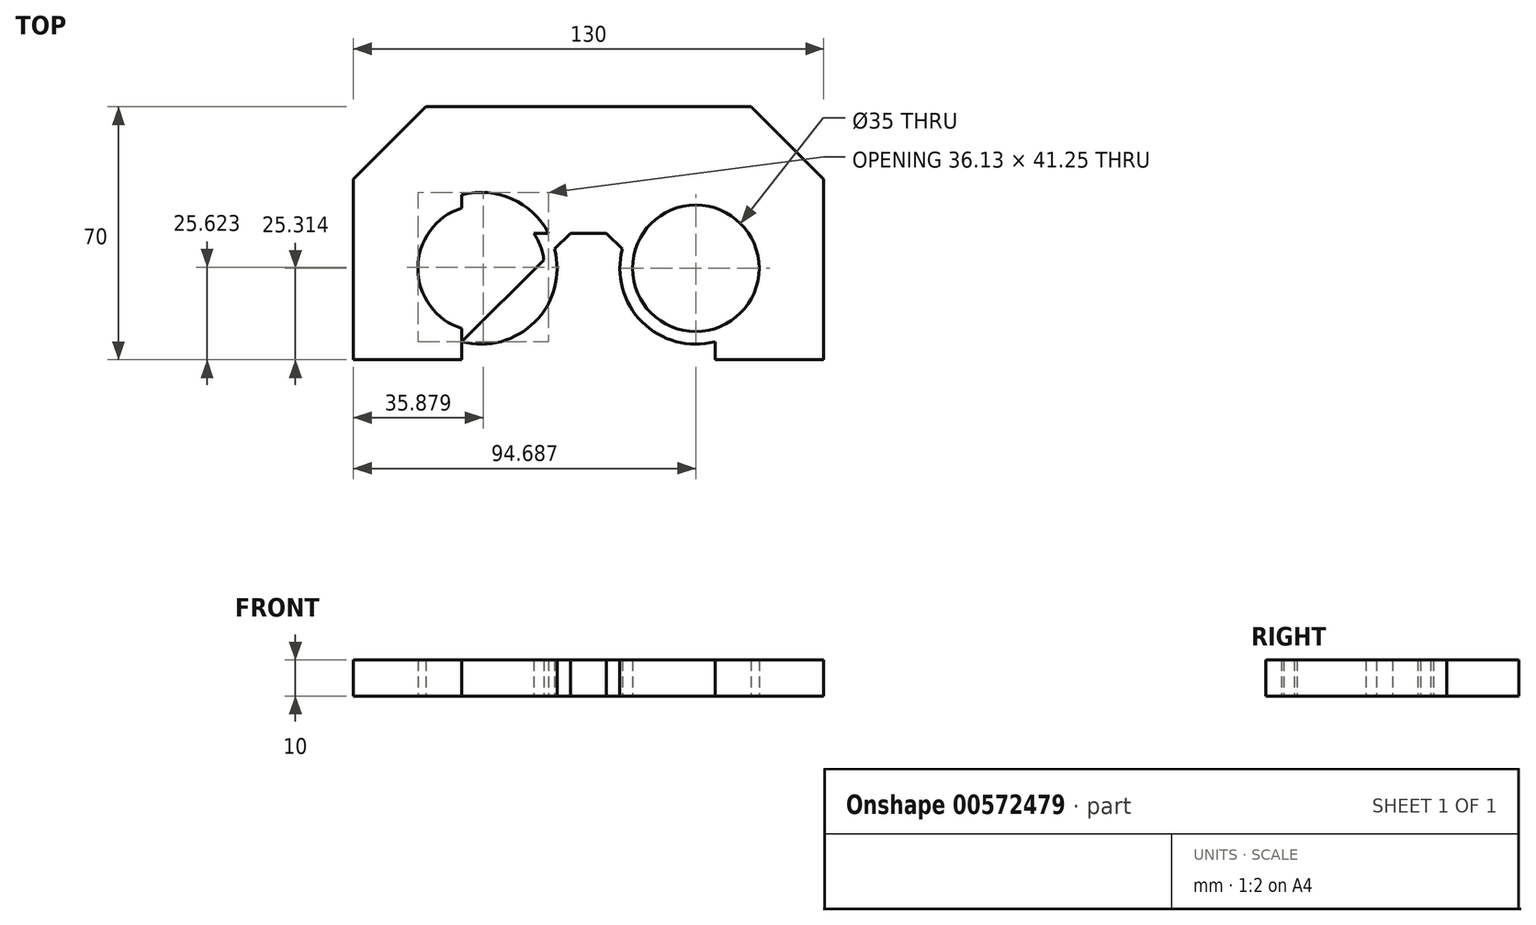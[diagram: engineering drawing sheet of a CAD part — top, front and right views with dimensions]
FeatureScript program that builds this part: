
annotation { "Feature Type Name" : "Feature", "Feature Type Description" : "" }
export const myFeature = defineFeature(function(context is Context, id is Id, definition is map)
    precondition{}
    {
        {
            var Q0;
            Q0=qCreatedBy(makeId("Top.planeOp"),FACE);
            var sketch = newSketch(context, id + "F0", { "sketchPlane" : qUnion([Q0])});
            skLineSegment(sketch, "E0.bottom", {"start": v(0, 0) * mm, "end": v(45, 0) * mm});
            skLineSegment(sketch, "E0.top", {"start": v(0, -35) * mm, "end": v(45, -35) * mm});
            skLineSegment(sketch, "E0.left", {"start": v(0, 0) * mm, "end": v(0, -35) * mm});
            skLineSegment(sketch, "E0.right", {"start": v(45, 0) * mm, "end": v(45, -35) * mm});
            skLineSegment(sketch, "E1.bottom", {"start": v(35, -20) * mm, "end": v(65, -20) * mm});
            skLineSegment(sketch, "E1.top", {"start": v(35, -70) * mm, "end": v(65, -70) * mm});
            skLineSegment(sketch, "E1.left", {"start": v(35, -20) * mm, "end": v(35, -70) * mm});
            skLineSegment(sketch, "E1.right", {"start": v(65, -20) * mm, "end": v(65, -70) * mm});
            skLineSegment(sketch, "E2", {"start": v(5, -35) * mm, "end": v(35, -65) * mm});
            skLineSegment(sketch, "E3", {"start": v(45, 0) * mm, "end": v(65, -20) * mm});
            skCircle(sketch, "E4", {"center": v(29.69, -44.69) * mm, "radius": 17.5 * mm});
            skCircle(sketch, "E5", {"center": v(29.69, -44.69) * mm, "radius": 21 * mm});
            skLineSegment(sketch, "E6.MirrorCS", {"start": v(-45, 0) * mm, "end": v(-45, -35) * mm});
            skCircle(sketch, "E7.MirrorC", {"center": v(-29.69, -44.69) * mm, "radius": 21 * mm});
            skCircle(sketch, "E8.MirrorC", {"center": v(-29.69, -44.69) * mm, "radius": 17.5 * mm});
            skLineSegment(sketch, "E9.MirrorCS", {"start": v(-45, 0) * mm, "end": v(-65, -20) * mm});
            skLineSegment(sketch, "E10.MirrorCS", {"start": v(-5, -35) * mm, "end": v(-35, -65) * mm});
            skLineSegment(sketch, "E11.MirrorCS", {"start": v(-65, -20) * mm, "end": v(-65, -70) * mm});
            skLineSegment(sketch, "E12.MirrorCS", {"start": v(-35, -20) * mm, "end": v(-35, -70) * mm});
            skLineSegment(sketch, "E13.MirrorCS", {"start": v(-35, -20) * mm, "end": v(-65, -20) * mm});
            skLineSegment(sketch, "E14.MirrorCS", {"start": v(0, 0) * mm, "end": v(-45, 0) * mm});
            skLineSegment(sketch, "E15.MirrorCS", {"start": v(0, -35) * mm, "end": v(-45, -35) * mm});
            skLineSegment(sketch, "E16.MirrorCS", {"start": v(-35, -70) * mm, "end": v(-65, -70) * mm});
            skSolve(sketch);
        }
        {
            var Q0;
            Q0 = qSketchRegion(id + "F0", true);
            var Q1;
            {var subQ0=sQuery(id+"F0.wireOp",EDGE,"E13.MirrorCS");var subQ1=sQuery(id+"F0.wireOp",EDGE,"E6.MirrorCS");var subQ2=makeQuery(id+"F0.imprint","INTERSECT",VERTEX,{"derivedFrom":[subQ1,subQ0]});Q1=makeQuery(id+"F0.imprint","IMPRINT",FACE,{"disambiguationData":[TD([[makeQuery(id+"F0.imprint","IMPRINT",EDGE,{"disambiguationData":[TD([[subQ2,-1.0]])],"derivedFrom":subQ1}),1.0]])]});}
            var Q2;
            {var subQ5=sQuery(id+"F0.wireOp",EDGE,"E15.MirrorCS");var subQ7=sQuery(id+"F0.wireOp",EDGE,"E6.MirrorCS");var subQ9=makeQuery(id+"F0.imprint","INTERSECT",VERTEX,{"derivedFrom":[subQ7,subQ5]});Q2=makeQuery(id+"F0.imprint","IMPRINT",FACE,{"disambiguationData":[TD([[makeQuery(id+"F0.imprint","IMPRINT",EDGE,{"disambiguationData":[TD([[subQ9,1.0]])],"derivedFrom":subQ7}),1.0]])]});}
            var Q3;
            {var subQ0=sQuery(id+"F0.wireOp",EDGE,"E12.MirrorCS");var subQ1=sQuery(id+"F0.wireOp",EDGE,"E7.MirrorC");var subQ2=makeQuery(id+"F0.imprint","INTERSECT",VERTEX,{"disambiguationData":[OD(1.0)],"derivedFrom":[subQ1,subQ0]});Q3=makeQuery(id+"F0.imprint","IMPRINT",FACE,{"disambiguationData":[TD([[makeQuery(id+"F0.imprint","IMPRINT",EDGE,{"disambiguationData":[TD([[subQ2,-1.0]])],"derivedFrom":subQ1}),-1.0]])]});}
            var Q4;
            {var subQ0=sQuery(id+"F0.wireOp",EDGE,"E10.MirrorCS");var subQ1=sQuery(id+"F0.wireOp",EDGE,"E8.MirrorC");var subQ2=makeQuery(id+"F0.imprint","INTERSECT",VERTEX,{"disambiguationData":[OD(1.0)],"derivedFrom":[subQ1,subQ0]});Q4=makeQuery(id+"F0.imprint","IMPRINT",FACE,{"disambiguationData":[TD([[makeQuery(id+"F0.imprint","IMPRINT",EDGE,{"disambiguationData":[TD([[subQ2,-1.0]])],"derivedFrom":subQ1}),1.0]])]});}
            var Q5;
            {var subQ0=sQuery(id+"F0.wireOp",EDGE,"E5");var subQ1=sQuery(id+"F0.wireOp",EDGE,"E0.top");var subQ2=makeQuery(id+"F0.imprint","INTERSECT",VERTEX,{"derivedFrom":[subQ1,subQ0]});Q5=makeQuery(id+"F0.imprint","IMPRINT",FACE,{"disambiguationData":[TD([[makeQuery(id+"F0.imprint","IMPRINT",EDGE,{"disambiguationData":[TD([[subQ2,-1.0]])],"derivedFrom":subQ1}),1.0]])]});}
            var Q6;
            {var subQ5=sQuery(id+"F0.wireOp",EDGE,"E0.right");var subQ6=sQuery(id+"F0.wireOp",EDGE,"E0.top");var subQ7=makeQuery(id+"F0.imprint","INTERSECT",VERTEX,{"derivedFrom":[subQ6,subQ5]});Q6=makeQuery(id+"F0.imprint","IMPRINT",FACE,{"disambiguationData":[TD([[makeQuery(id+"F0.imprint","IMPRINT",EDGE,{"disambiguationData":[TD([[subQ7,1.0]])],"derivedFrom":subQ6}),1.0]])]});}
            var Q7;
            {var subQ0=sQuery(id+"F0.wireOp",EDGE,"E1.bottom");var subQ1=sQuery(id+"F0.wireOp",EDGE,"E0.right");var subQ2=makeQuery(id+"F0.imprint","INTERSECT",VERTEX,{"derivedFrom":[subQ1,subQ0]});Q7=makeQuery(id+"F0.imprint","IMPRINT",FACE,{"disambiguationData":[TD([[makeQuery(id+"F0.imprint","IMPRINT",EDGE,{"disambiguationData":[TD([[subQ2,-1.0]])],"derivedFrom":subQ1}),-1.0]])]});}
            var Q8;
            {var subQ0=sQuery(id+"F0.wireOp",EDGE,"E2");var subQ1=sQuery(id+"F0.wireOp",EDGE,"E1.left");var subQ2=makeQuery(id+"F0.imprint","INTERSECT",VERTEX,{"derivedFrom":[subQ1,subQ0]});Q8=makeQuery(id+"F0.imprint","IMPRINT",FACE,{"disambiguationData":[TD([[makeQuery(id+"F0.imprint","IMPRINT",EDGE,{"disambiguationData":[TD([[subQ2,1.0]])],"derivedFrom":subQ1}),-1.0]])]});}
            extrude(context, id + "F1", {"entities" : qUnion([Q0, Q1, Q2, Q3, Q4, Q5, Q6, Q7, Q8]), "depth" : 10 * mm, "offsetDistance" : 25 * mm});
        }
    });
